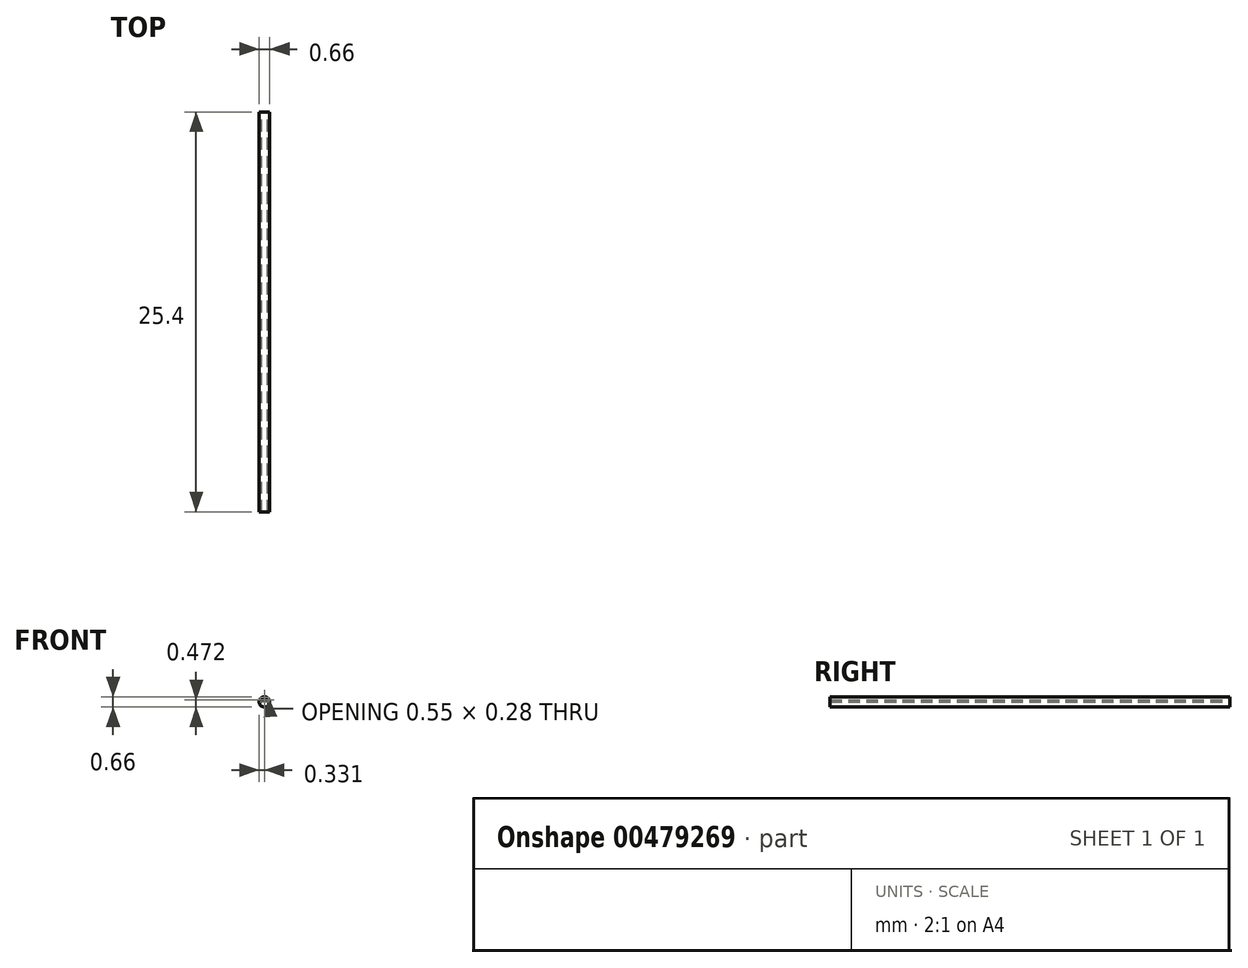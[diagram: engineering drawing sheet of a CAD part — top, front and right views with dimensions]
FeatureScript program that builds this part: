
annotation { "Feature Type Name" : "Feature", "Feature Type Description" : "" }
export const myFeature = defineFeature(function(context is Context, id is Id, definition is map)
    precondition{}
    {
        {
            var Q0;
            Q0=qCreatedBy(makeId("Front.planeOp"),FACE);
            var sketch = newSketch(context, id + "F0", { "sketchPlane" : qUnion([Q0])});
            skCircle(sketch, "E0", {"center": v(-0.05, 0.31) * mm, "radius": 0.04 * mm, "construction": true});
            skCircle(sketch, "E1", {"center": v(0, 0.22) * mm, "radius": 0.15 * mm, "construction": true});
            skCircle(sketch, "E2", {"center": v(-0.1, 0.25) * mm, "radius": 0.04 * mm, "construction": true});
            skCircle(sketch, "E3", {"center": v(0.02, 0.32) * mm, "radius": 0.04 * mm, "construction": true});
            skCircle(sketch, "E4", {"center": v(0.09, 0.28) * mm, "radius": 0.04 * mm, "construction": true});
            skCircle(sketch, "E5", {"center": v(0.1, 0.2) * mm, "radius": 0.04 * mm, "construction": true});
            skCircle(sketch, "E6", {"center": v(0.07, 0.14) * mm, "radius": 0.04 * mm, "construction": true});
            skCircle(sketch, "E7", {"center": v(-0.1, 0.18) * mm, "radius": 0.04 * mm, "construction": true});
            skCircle(sketch, "E8", {"center": v(0, 0.1) * mm, "radius": 0.04 * mm, "construction": true});
            skCircle(sketch, "E9", {"center": v(0.02, 0.24) * mm, "radius": 0.04 * mm, "construction": true});
            skCircle(sketch, "E10", {"center": v(-0.02, 0.18) * mm, "radius": 0.04 * mm, "construction": true});
            skCircle(sketch, "E11", {"center": v(0, 0.22) * mm, "radius": 0.17 * mm, "construction": true});
            skCircle(sketch, "E12", {"center": v(0, -0.17) * mm, "radius": 0.22 * mm, "construction": true});
            skCircle(sketch, "E13", {"center": v(0, -0.17) * mm, "radius": 0.2 * mm, "construction": true});
            skCircle(sketch, "E14", {"center": v(0, 0) * mm, "radius": 0.39 * mm, "construction": true});
            skCircle(sketch, "E15", {"center": v(-1.17, 0.2) * mm, "radius": 0.33 * mm});
            skCircle(sketch, "E16", {"center": v(-1.17, 0.08) * mm, "radius": 0.22 * mm});
            skCircle(sketch, "E17", {"center": v(-1.17, 0.08) * mm, "radius": 0.2 * mm, "construction": true});
            skArc(sketch, "E18", {"start": v(-0.96, 0.2) * mm, "mid": v(-1.15, 0.32) * mm, "end": v(-1.37, 0.22) * mm});
            skArc(sketch, "E19", {"start": v(-0.9, 0.23) * mm, "mid": v(-1.16, 0.47) * mm, "end": v(-1.44, 0.26) * mm});
            skArc(sketch, "E20", {"start": v(-1.44, 0.26) * mm, "mid": v(-1.41, 0.23) * mm, "end": v(-1.37, 0.22) * mm});
            skArc(sketch, "E21", {"start": v(-0.96, 0.2) * mm, "mid": v(-0.92, 0.2) * mm, "end": v(-0.9, 0.23) * mm});
            skPoint(sketch, "E22.orphan", {"position": v(-1.41, 0.05) * mm});
            skCircle(sketch, "E23", {"center": v(-1.38, 0.28) * mm, "radius": 0.04 * mm, "construction": true});
            skCircle(sketch, "E24", {"center": v(-0.96, 0.25) * mm, "radius": 0.04 * mm, "construction": true});
            skCircle(sketch, "E25", {"center": v(-1.34, 0.36) * mm, "radius": 0.04 * mm, "construction": true});
            skCircle(sketch, "E26", {"center": v(-1.28, 0.41) * mm, "radius": 0.04 * mm, "construction": true});
            skCircle(sketch, "E27", {"center": v(-1.19, 0.43) * mm, "radius": 0.04 * mm, "construction": true});
            skCircle(sketch, "E28", {"center": v(-1.08, 0.41) * mm, "radius": 0.04 * mm, "construction": true});
            skCircle(sketch, "E29", {"center": v(-1.22, 0.36) * mm, "radius": 0.04 * mm, "construction": true});
            skCircle(sketch, "E30", {"center": v(-0.98, 0.33) * mm, "radius": 0.04 * mm, "construction": true});
            skCircle(sketch, "E31", {"center": v(-1.14, 0.36) * mm, "radius": 0.04 * mm, "construction": true});
            skCircle(sketch, "E32", {"center": v(-1.06, 0.34) * mm, "radius": 0.04 * mm, "construction": true});
            skSolve(sketch);
        }
        {
            var Q0;
            Q0=makeQuery(id+"F0.imprint","IMPRINT",FACE,{"disambiguationData":[TD([[makeQuery(id+"F0.imprint","IMPRINT",EDGE,{"derivedFrom":sQuery(id+"F0.wireOp",EDGE,"E15")}),1.0]])]});
            var Q1;
            Q1=makeQuery(id+"F0.imprint","IMPRINT",FACE,{"disambiguationData":[TD([[makeQuery(id+"F0.imprint","IMPRINT",EDGE,{"derivedFrom":sQuery(id+"F0.wireOp",EDGE,"E16")}),1.0]])]});
            extrude(context, id + "F1", {"entities" : qUnion([Q0, Q1]), "depth" : 25.4 * mm});
        }
    });
